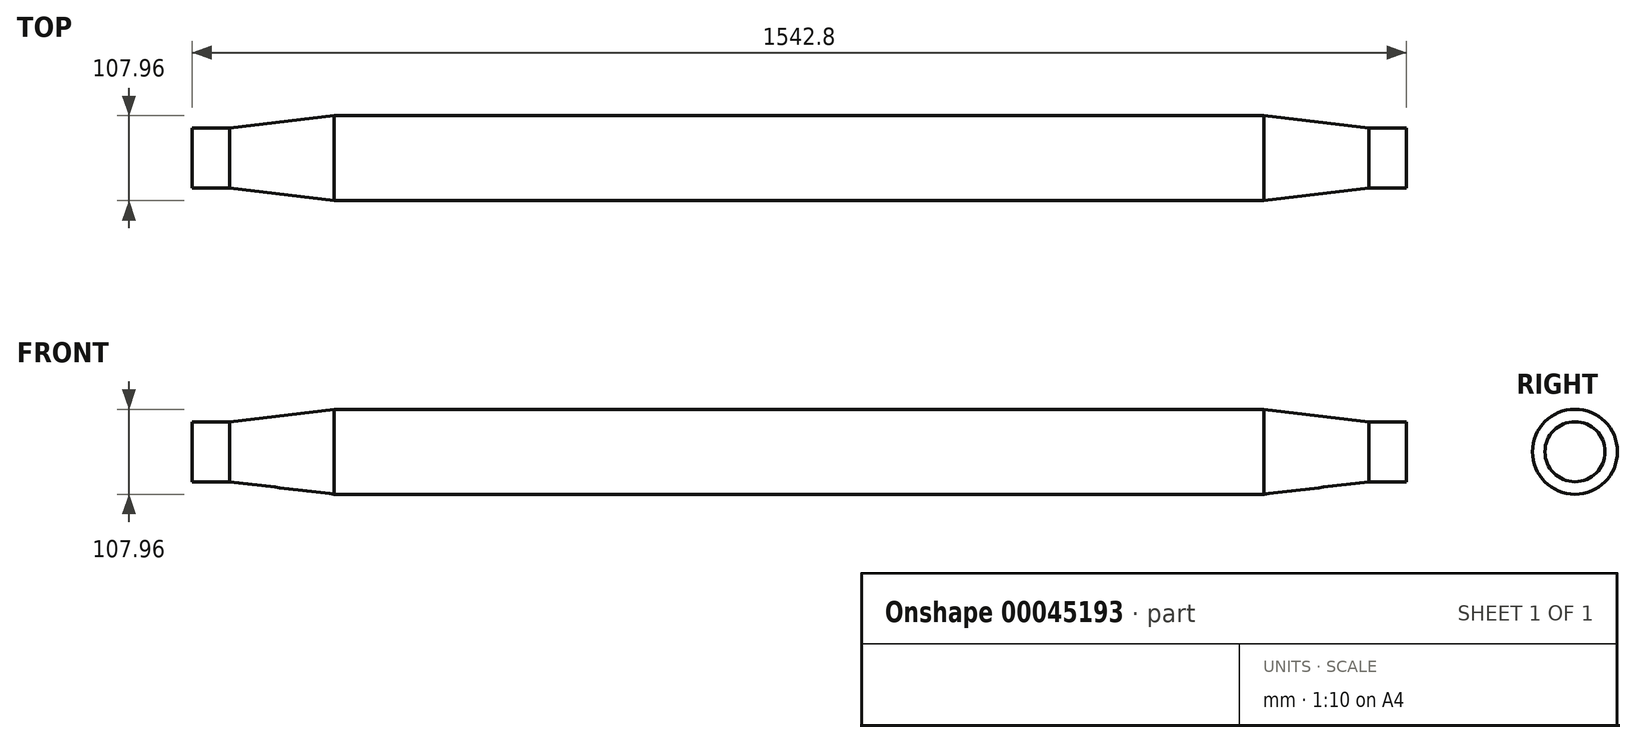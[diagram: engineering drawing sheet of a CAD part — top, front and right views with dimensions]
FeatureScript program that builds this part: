
annotation { "Feature Type Name" : "Feature", "Feature Type Description" : "" }
export const myFeature = defineFeature(function(context is Context, id is Id, definition is map)
    precondition{}
    {
        {
            var Q0;
            Q0=qCreatedBy(makeId("Right.planeOp"),FACE);
            var sketch = newSketch(context, id + "F0", { "sketchPlane" : qUnion([Q0])});
            skCircle(sketch, "E0", {"center": v(0, 0) * mm, "radius": 53.97 * mm});
            skSolve(sketch);
        }
        {
            var Q0;
            Q0 = qSketchRegion(id + "F0", true);
            extrude(context, id + "F1", {"entities" : qUnion([Q0]), "endBound" : BoundingType.SYMMETRIC, "depth" : 1181.1 * mm});
        }
        {
            var Q0;
            Q0=makeQuery(id+"F1.opExtrude","CAP_FACE",FACE,{"disambiguationData":[OSD([sQuery(id+"F0.wireOp",EDGE,"E0")])],"isStart":false});
            cPlane(context, id + "F2", {"entities" : qUnion([Q0]), "cplaneType" : CPlaneType.OFFSET, "offset" : 180.85 * mm, "width" : 152.4 * mm, "height" : 152.4 * mm});
        }
        {
            var Q0;
            Q0=qCreatedBy(id+"F2.planeOp",FACE);
            var sketch = newSketch(context, id + "F3", { "sketchPlane" : qUnion([Q0])});
            skCircle(sketch, "E1", {"center": v(0, 0) * mm, "radius": 38.1 * mm});
            skSolve(sketch);
        }
        {
            var Q0;
            Q0 = qSketchRegion(id + "F3", true);
            extrude(context, id + "F4", {"entities" : qUnion([Q0]), "oppositeDirection" : true, "depth" : 47.75 * mm});
        }
        {
            var Q0;
            Q0=makeQuery(id+"F4.opExtrude","SWEPT_BODY",BODY,{"disambiguationData":[OSD([sQuery(id+"F3.wireOp",EDGE,"E1")])]});
            var Q1;
            Q1=qCreatedBy(makeId("Right.planeOp"),FACE);
            mirror(context, id + "F5", {"entities" : qUnion([Q0]), "mirrorPlane" : qUnion([Q1])});
        }
        {
            var Q0;
            Q0=makeQuery(id+"F1.opExtrude","CAP_FACE",FACE,{"disambiguationData":[OSD([sQuery(id+"F0.wireOp",EDGE,"E0")])],"isStart":false});
            var Q1;
            Q1=makeQuery(id+"F4.opExtrude","CAP_FACE",FACE,{"disambiguationData":[OSD([sQuery(id+"F3.wireOp",EDGE,"E1")])],"isStart":false});
            loft(context, id + "F6", {"sheetProfilesArray" : [{ "sheetProfileEntities" : qUnion([Q0]) }, { "sheetProfileEntities" : qUnion([Q1]) }]});
        }
        {
            var Q0;
            Q0=makeQuery(id+"F1.opExtrude","CAP_FACE",FACE,{"disambiguationData":[OSD([sQuery(id+"F0.wireOp",EDGE,"E0")])],"isStart":true});
            var Q1;
            Q1=makeQuery(id+"F5.opPattern","COPY",FACE,{"derivedFrom":makeQuery(id+"F4.opExtrude","CAP_FACE",FACE,{"disambiguationData":[OSD([sQuery(id+"F3.wireOp",EDGE,"E1")])],"isStart":false}),"instanceName":"1"});
            loft(context, id + "F7", {"sheetProfilesArray" : [{ "sheetProfileEntities" : qUnion([Q0]) }, { "sheetProfileEntities" : qUnion([Q1]) }]});
        }
    });
